# Revit family: Trane_TVR_Outdoor_4TVH0140(155_170)FE000AA_380~415V(50_60Hz)
name_source: partatom
category: Equipamento mecânico
units: mm (PartAtom-declared; Revit-internal decimal feet)

## family parameters
Com base no plano de trabalho = Não
Compartilhado = Não
Corte com vazios quando carregada = Não
Cota do conector redondo = Utilizar diâmetro
Número OmniClass = 23.75.00.00
Ponto de cálculo do ambiente = Não
Sempre na vertical = Sim
Tipo de parte = Normal
Título OmniClass = Climate Control (HVAC)

## types (3) — shared parameters
Air Flow = 13000.00 m³/h
Casing color = white
Compressor = 1
Condensation = Air
Depth = 850  [stored 2.78871 ft]
Descrição = High efficiency air cooled
Fabricante = Trane
Gas = R410A
Gas pipe = 31.8  [stored 0.104331 ft]
Height = 1635  [stored 5.36417 ft]
Installation = Outdoor installation
Machine material = Galvanized Steel
Maximum Fuse Amps = 40 A
Power supply = 380-415V 3N~50Hz/60Hz
Series = ULTRA S
URL = https://www.trane.com
Width = 1340  [stored 4.39633 ft]
clearance access behind = 1000  [stored 3.28084 ft]
clearance access front = 1000  [stored 3.28084 ft]
clearance access left = 1000  [stored 3.28084 ft]
clearance access right = 1000  [stored 3.28084 ft]

## per-type parameters (varying)
| type | Cooling Capacity | Cooling Power Input | Heating Capacity | Heating Power Input | Liquid pipe | Minimum Circuit Amps | Net Weight |
| 4TVH0140FE000AA | 40.00 kW | 10.61 kW | 40.00 kW | 9.11 kW | 15.9  [stored 0.0521654 ft] | 33 A | 277.00 kg |
| 4TVH0155FE000AA | 45.00 kW | 12.47 kW | 45.00 kW | 10.51 kW | 15.9  [stored 0.0521654 ft] | 33 A | 277.00 kg |
| 4TVH0170FE000AA | 50.00 kW | 13.48 kW | 50.00 kW | 11.47 kW | 19.1  [stored 0.062664 ft] | 35 A | 295.00 kg |

note: column(s) folded — value = type name in every type: Modelo

note: [stored X ft] marks values corroborated as IEEE doubles in the binary element streams (Revit-internal decimal feet)

## geometry (parser evidence)
native form markers: Blend x2, Sweep x3
no freeform markers — native parametric forms only
